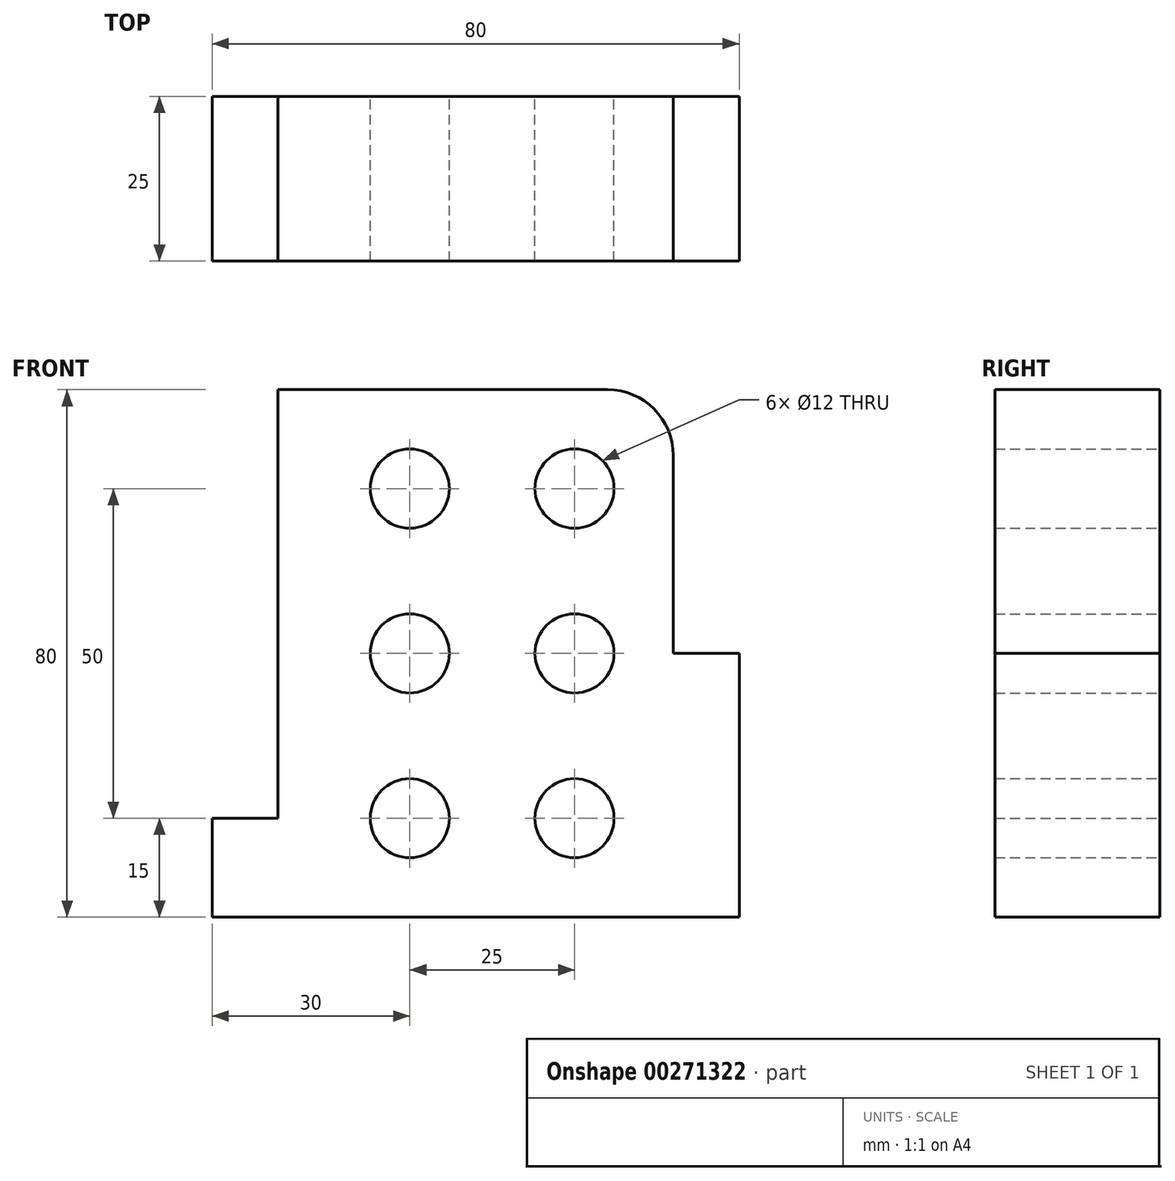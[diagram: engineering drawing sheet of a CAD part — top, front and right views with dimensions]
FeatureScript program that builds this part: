
annotation { "Feature Type Name" : "Feature", "Feature Type Description" : "" }
export const myFeature = defineFeature(function(context is Context, id is Id, definition is map)
    precondition{}
    {
        {
            var Q0;
            Q0=qCreatedBy(makeId("Front.planeOp"),FACE);
            var sketch = newSketch(context, id + "F0", { "sketchPlane" : qUnion([Q0])});
            skLineSegment(sketch, "E0", {"start": v(0, 0) * mm, "end": v(80, 0) * mm});
            skLineSegment(sketch, "E1", {"start": v(80, 0) * mm, "end": v(80, 40) * mm});
            skLineSegment(sketch, "E2", {"start": v(80, 40) * mm, "end": v(70, 40) * mm});
            skLineSegment(sketch, "E3", {"start": v(70, 40) * mm, "end": v(70, 70) * mm});
            skLineSegment(sketch, "E4", {"start": v(0, 0) * mm, "end": v(0, 15) * mm});
            skLineSegment(sketch, "E5", {"start": v(0, 15) * mm, "end": v(10, 15) * mm});
            skLineSegment(sketch, "E6", {"start": v(10, 15) * mm, "end": v(10, 80) * mm});
            skLineSegment(sketch, "E7", {"start": v(10, 80) * mm, "end": v(60, 80) * mm});
            skArc(sketch, "E8", {"start": v(70, 70) * mm, "mid": v(67.07, 77.07) * mm, "end": v(60, 80) * mm});
            skCircle(sketch, "E9", {"center": v(55, 65) * mm, "radius": 6 * mm});
            skCircle(sketch, "E10", {"center": v(30, 65) * mm, "radius": 6 * mm});
            skCircle(sketch, "E11", {"center": v(30, 40) * mm, "radius": 6 * mm});
            skCircle(sketch, "E12", {"center": v(55, 40) * mm, "radius": 6 * mm});
            skCircle(sketch, "E13", {"center": v(30, 15) * mm, "radius": 6 * mm});
            skCircle(sketch, "E14", {"center": v(55, 15) * mm, "radius": 6 * mm});
            skSolve(sketch);
        }
        {
            var Q0;
            Q0 = qSketchRegion(id + "F0", true);
            extrude(context, id + "F1", {"entities" : qUnion([Q0]), "depth" : 25 * mm});
        }
    });
